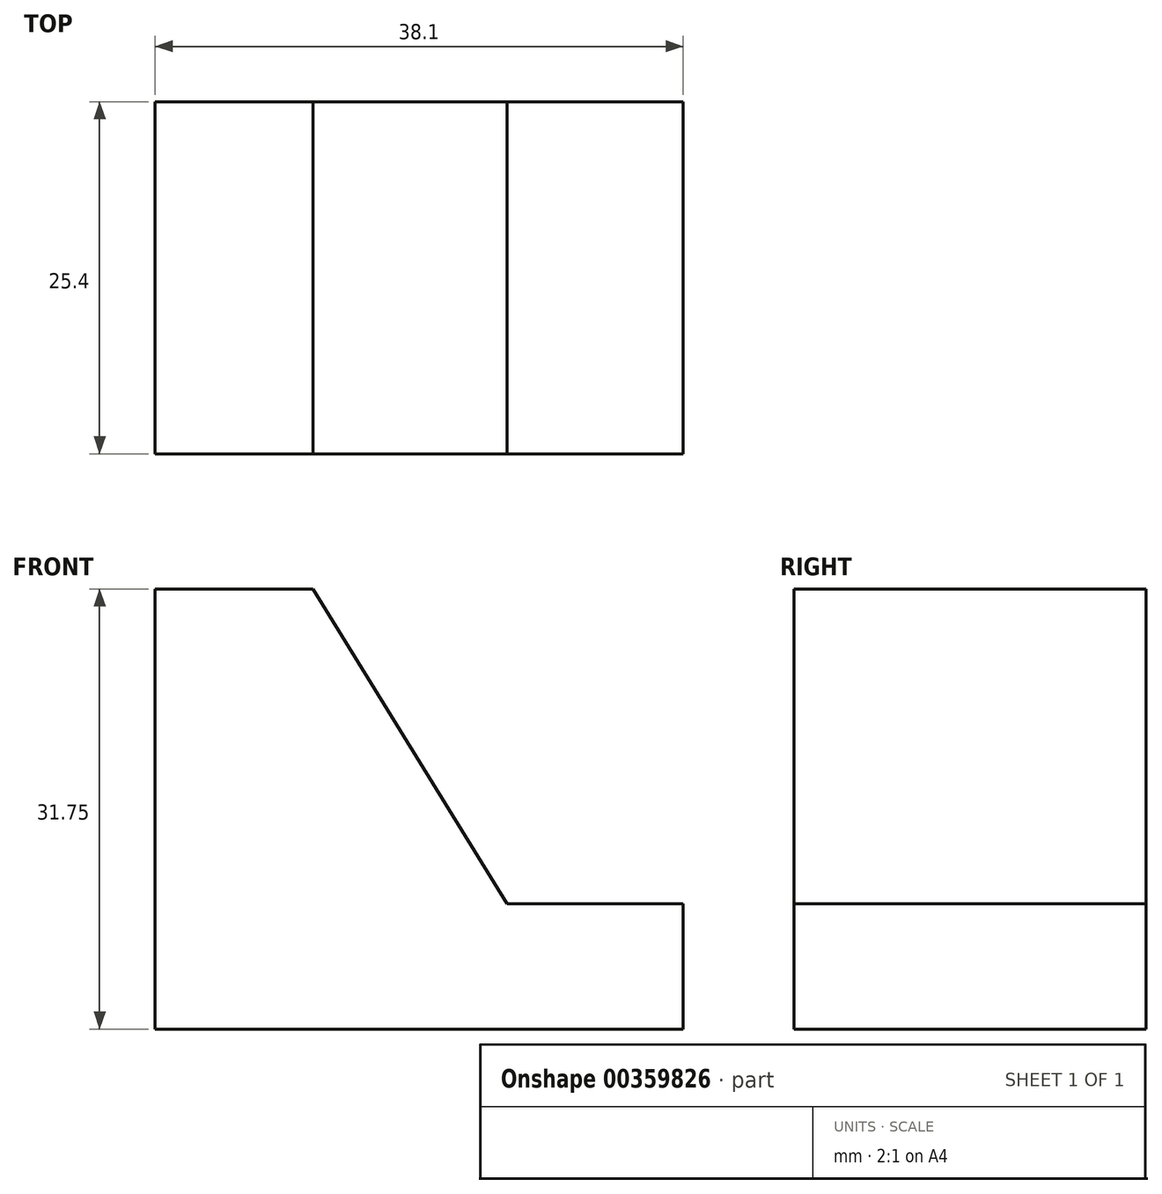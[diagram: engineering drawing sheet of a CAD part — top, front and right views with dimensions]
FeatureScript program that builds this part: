
annotation { "Feature Type Name" : "Feature", "Feature Type Description" : "" }
export const myFeature = defineFeature(function(context is Context, id is Id, definition is map)
    precondition{}
    {
        {
            var Q0;
            Q0=qCreatedBy(makeId("Front.planeOp"),FACE);
            var sketch = newSketch(context, id + "F0", { "sketchPlane" : qUnion([Q0])});
            skLineSegment(sketch, "E0", {"start": v(0, 0) * mm, "end": v(38.1, 0) * mm});
            skLineSegment(sketch, "E1", {"start": v(38.1, 0) * mm, "end": v(38.1, 31.75) * mm});
            skLineSegment(sketch, "E2", {"start": v(38.1, 31.75) * mm, "end": v(0, 31.75) * mm});
            skLineSegment(sketch, "E3", {"start": v(0, 31.75) * mm, "end": v(0, 0) * mm});
            skSolve(sketch);
        }
        {
            var Q0;
            Q0=makeQuery(id+"F0.imprint","IMPRINT",FACE,{"disambiguationData":[TD([[makeQuery(id+"F0.imprint","IMPRINT",EDGE,{"derivedFrom":sQuery(id+"F0.wireOp",EDGE,"E0")}),1.0]])]});
            extrude(context, id + "F1", {"entities" : qUnion([Q0]), "depth" : 25.4 * mm});
        }
        {
            var Q0;
            Q0=makeQuery(id+"F1.opExtrude","CAP_FACE",FACE,{"disambiguationData":[OSD([sQuery(id+"F0.wireOp",EDGE,"E0"),sQuery(id+"F0.wireOp",EDGE,"E1"),sQuery(id+"F0.wireOp",EDGE,"E2"),sQuery(id+"F0.wireOp",EDGE,"E3")])],"isStart":false});
            var sketch = newSketch(context, id + "F2", { "sketchPlane" : qUnion([Q0])});
            skLineSegment(sketch, "E4", {"start": v(11.4, 31.75) * mm, "end": v(25.4, 9.04) * mm});
            skLineSegment(sketch, "E5", {"start": v(25.4, 9.04) * mm, "end": v(38.1, 9.04) * mm});
            skSolve(sketch);
        }
        {
            var Q0;
            Q0 = qSketchRegion(id + "F2", true);
            var Q1;
            {var subQ0=sQuery(id+"F2.wireOp",EDGE,"E4");Q1=makeQuery(id+"F2.imprint","IMPRINT",FACE,{"disambiguationData":[TD([[makeQuery(id+"F2.imprint","IMPRINT",EDGE,{"derivedFrom":subQ0}),1.0]])]});}
            extrude(context, id + "F3", {"entities" : qUnion([Q0, Q1]), "operationType" : NewBodyOperationType.REMOVE, "oppositeDirection" : true, "depth" : 25.4 * mm});
        }
    });
